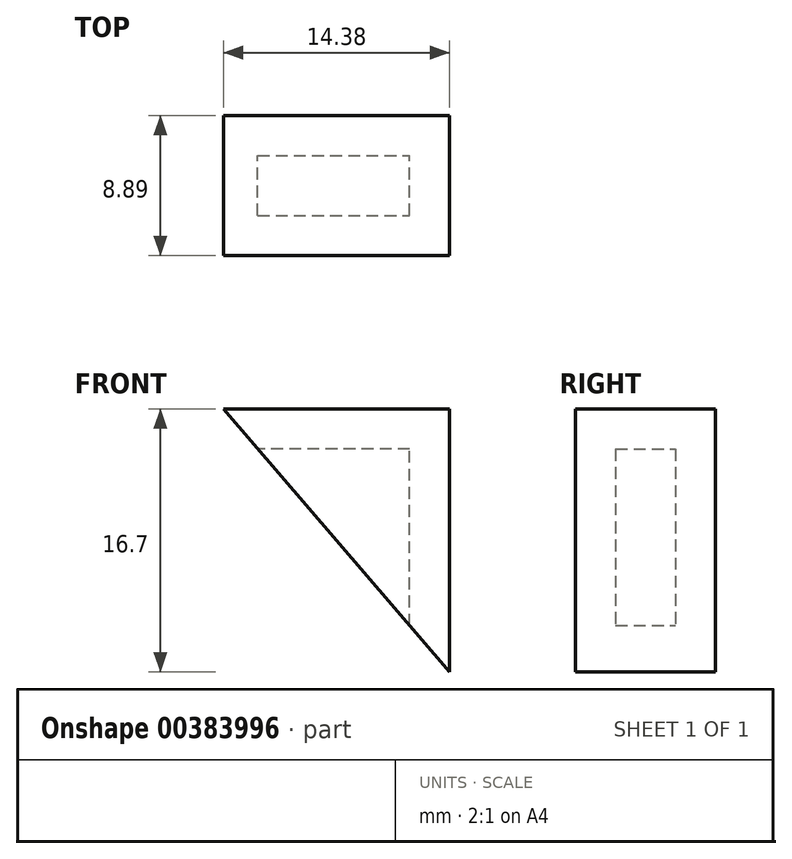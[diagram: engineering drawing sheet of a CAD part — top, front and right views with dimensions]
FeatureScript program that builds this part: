
annotation { "Feature Type Name" : "Feature", "Feature Type Description" : "" }
export const myFeature = defineFeature(function(context is Context, id is Id, definition is map)
    precondition{}
    {
        {
            var Q0;
            Q0=qCreatedBy(makeId("Front.planeOp"),FACE);
            var sketch = newSketch(context, id + "F0", { "sketchPlane" : qUnion([Q0])});
            skLineSegment(sketch, "E0", {"start": v(0, 0) * mm, "end": v(0, 16.7) * mm});
            skLineSegment(sketch, "E1", {"start": v(0, 16.7) * mm, "end": v(-14.38, 16.7) * mm});
            skLineSegment(sketch, "E2", {"start": v(-14.38, 16.7) * mm, "end": v(0, 0) * mm});
            skSolve(sketch);
        }
        {
            var Q0;
            Q0=makeQuery(id+"F0.imprint","IMPRINT",FACE,{"disambiguationData":[TD([[makeQuery(id+"F0.imprint","IMPRINT",EDGE,{"derivedFrom":sQuery(id+"F0.wireOp",EDGE,"E0")}),1.0]])]});
            extrude(context, id + "F1", {"entities" : qUnion([Q0]), "depth" : 8.9 * mm, "offsetDistance" : 25.4 * mm});
        }
        {
            var Q0;
            Q0=makeQuery(id+"F1.opExtrude","SWEPT_FACE",FACE,{"disambiguationData":[OSD([sQuery(id+"F0.wireOp",EDGE,"E2")])]});
            shell(context, id + "F2", {"entities" : qUnion([Q0]), "thickness" : 2.54 * mm});
        }
    });
